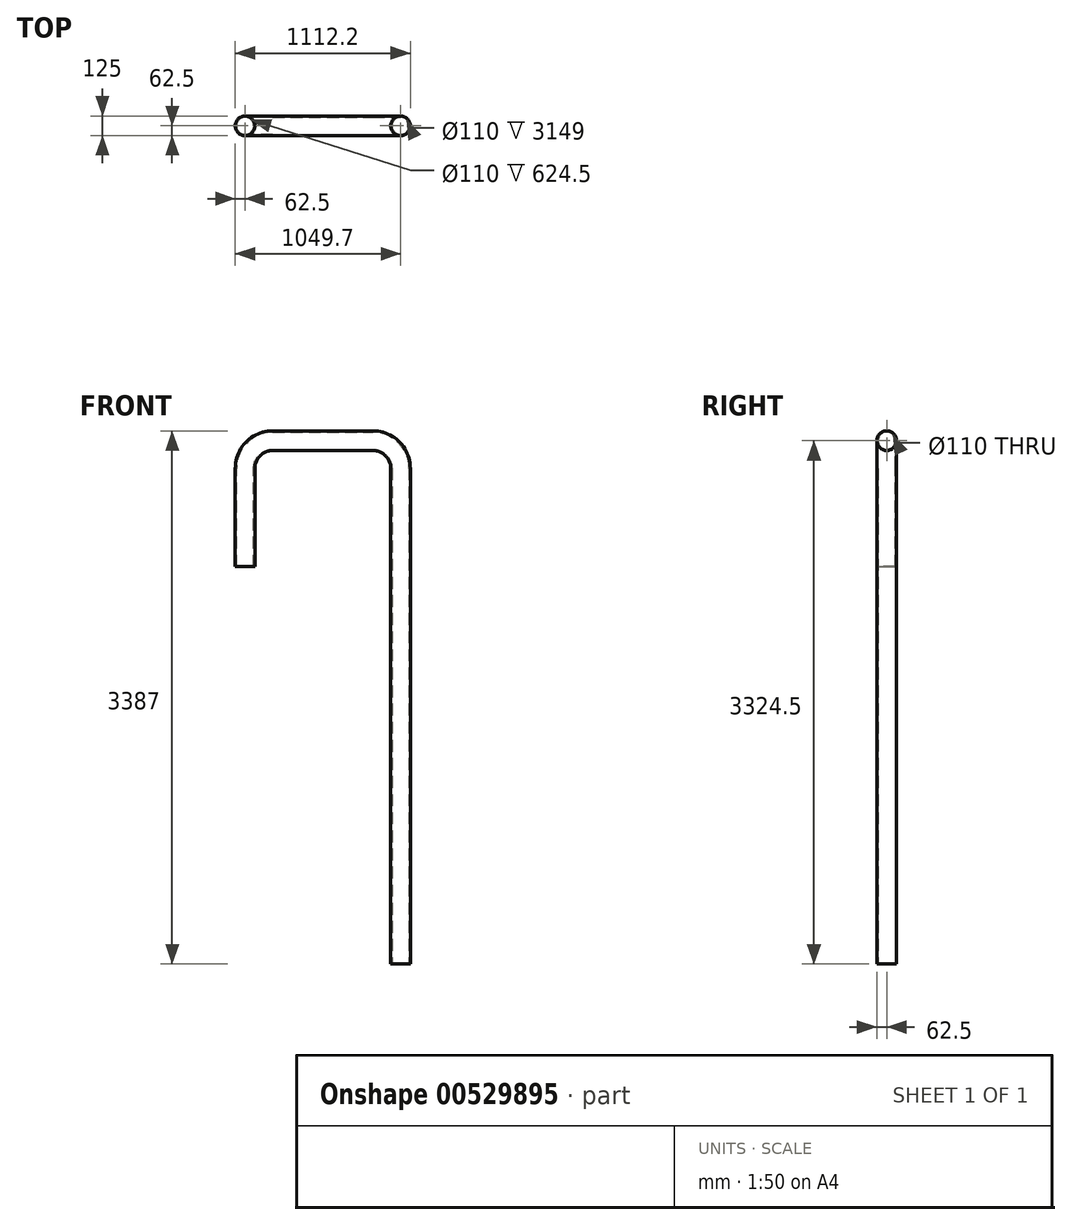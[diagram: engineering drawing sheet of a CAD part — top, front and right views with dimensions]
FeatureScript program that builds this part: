
annotation { "Feature Type Name" : "Feature", "Feature Type Description" : "" }
export const myFeature = defineFeature(function(context is Context, id is Id, definition is map)
    precondition{}
    {
        {
            var Q0;
            Q0=qCreatedBy(makeId("Front.planeOp"),FACE);
            var sketch = newSketch(context, id + "F0", { "sketchPlane" : qUnion([Q0])});
            skLineSegment(sketch, "E0", {"start": v(0, 0) * mm, "end": v(0, 624.5) * mm});
            skLineSegment(sketch, "E1", {"start": v(175.5, 800) * mm, "end": v(811.7, 800) * mm});
            skLineSegment(sketch, "E2", {"start": v(987.2, 624.5) * mm, "end": v(987.2, -2352.75) * mm});
            skPoint(sketch, "E3.visualSharp", {"position": v(0, 800) * mm});
            skArc(sketch, "E3.filletArc", {"start": v(175.5, 800) * mm, "mid": v(51.4, 748.6) * mm, "end": v(0, 624.5) * mm});
            skPoint(sketch, "E4.visualSharp", {"position": v(987.2, 800) * mm});
            skArc(sketch, "E4.filletArc", {"start": v(987.2, 624.5) * mm, "mid": v(935.8, 748.6) * mm, "end": v(811.7, 800) * mm});
            skSolve(sketch);
        }
        {
            var Q0;
            Q0=qCreatedBy(makeId("Front.planeOp"),FACE);
            var Q1;
            Q1=sQuery(id+"F0.wireOp",EDGE,"E2");
            cPlane(context, id + "F1", {"entities" : qUnion([Q0, Q1]), "cplaneType" : CPlaneType.LINE_ANGLE, "offset" : 25 * mm, "angle" : 330 * degree, "width" : 150 * mm, "height" : 150 * mm});
        }
        {
            var Q0;
            Q0=qCreatedBy(id+"F1.planeOp",FACE);
            var sketch = newSketch(context, id + "F2", { "sketchPlane" : qUnion([Q0])});
            skLineSegment(sketch, "E5.0", {"start": v(-854.94, 624.5) * mm, "end": v(-854.94, -2524.5) * mm});
            skPoint(sketch, "E6.visualSharp", {"position": v(-854.94, -2352.75) * mm});
            skSolve(sketch);
        }
        {
            var Q0;
            Q0=qCreatedBy(makeId("Top.planeOp"),FACE);
            var sketch = newSketch(context, id + "F3", { "sketchPlane" : qUnion([Q0])});
            skCircle(sketch, "E7", {"center": v(0, 0) * mm, "radius": 62.5 * mm});
            skCircle(sketch, "E8", {"center": v(0, 0) * mm, "radius": 55 * mm});
            skSolve(sketch);
        }
        {
            var Q0;
            Q0=makeQuery(id+"F3.imprint","IMPRINT",FACE,{"disambiguationData":[TD([[makeQuery(id+"F3.imprint","IMPRINT",EDGE,{"derivedFrom":sQuery(id+"F3.wireOp",EDGE,"E7")}),1.0]])]});
            var Q1;
            Q1=sQuery(id+"F0.wireOp",EDGE,"E0");
            var Q2;
            Q2=sQuery(id+"F0.wireOp",EDGE,"E3.filletArc");
            var Q3;
            Q3=sQuery(id+"F0.wireOp",EDGE,"E1");
            var Q4;
            Q4=sQuery(id+"F0.wireOp",EDGE,"E4.filletArc");
            var Q5;
            Q5=sQuery(id+"F2.wireOp",EDGE,"E5.0");
            var Q6;
            Q6=sQuery(id+"F2.wireOp",EDGE,"E6.filletArc");
            var Q7;
            Q7=sQuery(id+"F2.wireOp",EDGE,"WXx5i54O-1ZkQ-s0co-EDoO-J2Ul0ai4V1Lk");
            sweep(context, id + "F4", {"profiles" : qUnion([Q0]), "path" : qUnion([Q1, Q2, Q3, Q4, Q5, Q6, Q7])});
        }
        {
            var Q0;
            Q0=qCreatedBy(id+"F1.planeOp",FACE);
            var sketch = newSketch(context, id + "F5", { "sketchPlane" : qUnion([Q0])});
            skLineSegment(sketch, "E9", {"start": v(1624.83, -2713.44) * mm, "end": v(-2635.56, -2713.44) * mm, "construction": true});
            skSolve(sketch);
        }
    });
